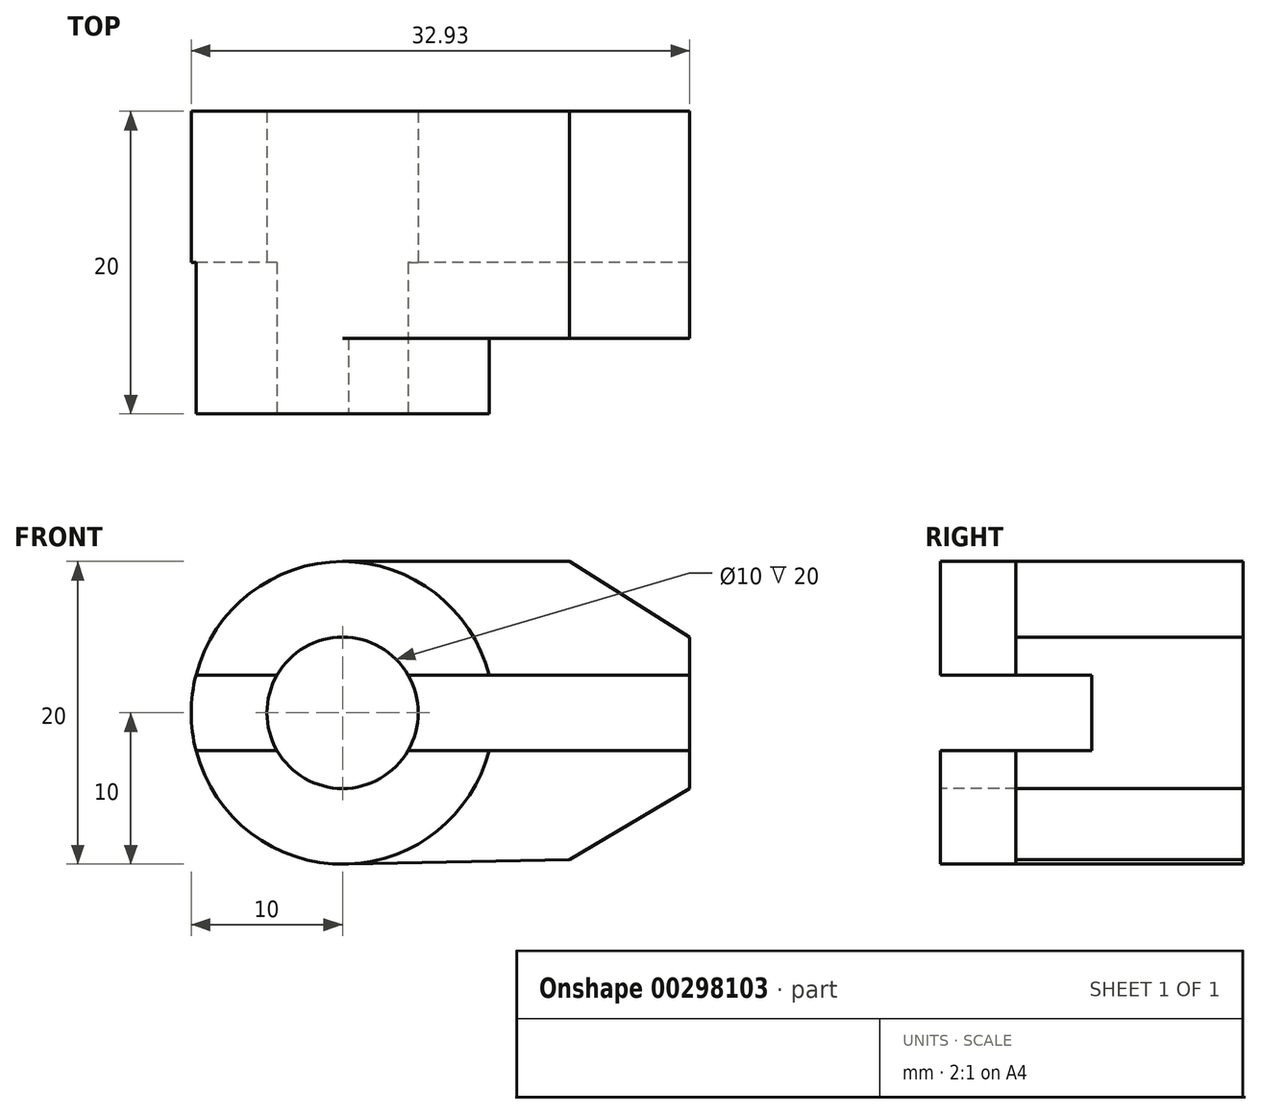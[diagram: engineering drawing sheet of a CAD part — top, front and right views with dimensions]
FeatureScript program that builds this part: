
annotation { "Feature Type Name" : "Feature", "Feature Type Description" : "" }
export const myFeature = defineFeature(function(context is Context, id is Id, definition is map)
    precondition{}
    {
        {
            var Q0;
            Q0=qCreatedBy(makeId("Front.planeOp"),FACE);
            var sketch = newSketch(context, id + "F0", { "sketchPlane" : qUnion([Q0])});
            skCircle(sketch, "E0", {"center": v(0, 0) * mm, "radius": 10 * mm});
            skLineSegment(sketch, "E1", {"start": v(0, 10) * mm, "end": v(15, 10) * mm});
            skPoint(sketch, "E2.end.orphan", {"position": v(0, -10) * mm});
            skLineSegment(sketch, "E3", {"start": v(0, -10) * mm, "end": v(15, -9.7) * mm});
            skLineSegment(sketch, "E4", {"start": v(22.93, 0) * mm, "end": v(22.93, 5) * mm});
            skLineSegment(sketch, "E5", {"start": v(22.93, 5) * mm, "end": v(22.93, 0) * mm});
            skLineSegment(sketch, "E6", {"start": v(22.93, -5) * mm, "end": v(22.93, 0) * mm});
            skLineSegment(sketch, "E7", {"start": v(15, 10) * mm, "end": v(22.93, 5) * mm});
            skLineSegment(sketch, "E8", {"start": v(15, -9.7) * mm, "end": v(22.93, -5) * mm});
            skSolve(sketch);
        }
        {
            var Q0;
            {var subQ0=sQuery(id+"F0.wireOp",EDGE,"E0");var subQ1=makeQuery(id+"F0.imprint","INTERSECT",VERTEX,{"derivedFrom":[subQ0,sQuery(id+"F0.wireOp",EDGE,"E1")]});Q0=makeQuery(id+"F0.imprint","IMPRINT",FACE,{"disambiguationData":[TD([[makeQuery(id+"F0.imprint","IMPRINT",EDGE,{"disambiguationData":[TD([[subQ1,-1.0]])],"derivedFrom":subQ0}),1.0]])]});}
            extrude(context, id + "F1", {"entities" : qUnion([Q0]), "oppositeDirection" : true, "depth" : 20 * mm});
        }
        {
            var Q0;
            {var subQ4=sQuery(id+"F0.wireOp",EDGE,"E1");Q0=makeQuery(id+"F0.imprint","IMPRINT",FACE,{"disambiguationData":[TD([[makeQuery(id+"F0.imprint","IMPRINT",EDGE,{"derivedFrom":subQ4}),-1.0]])]});}
            extrude(context, id + "F2", {"entities" : qUnion([Q0]), "operationType" : NewBodyOperationType.ADD, "oppositeDirection" : true, "depth" : 20 * mm});
        }
        {
            var Q0;
            {var subQ4=sQuery(id+"F0.wireOp",EDGE,"E1");Q0=makeQuery(id+"F0.imprint","IMPRINT",FACE,{"disambiguationData":[TD([[makeQuery(id+"F0.imprint","IMPRINT",EDGE,{"derivedFrom":subQ4}),-1.0]])]});}
            var sketch = newSketch(context, id + "F3", { "sketchPlane" : qUnion([Q0])});
            skArc(sketch, "E9", {"start": v(0, 10) * mm, "mid": v(10, 0) * mm, "end": v(0, -10) * mm});
            skLineSegment(sketch, "E10", {"start": v(0, 10) * mm, "end": v(15, 10) * mm});
            skLineSegment(sketch, "E11", {"start": v(15, 10) * mm, "end": v(22.93, 5) * mm});
            skLineSegment(sketch, "E12", {"start": v(22.93, 5) * mm, "end": v(22.93, -5) * mm});
            skLineSegment(sketch, "E13", {"start": v(22.93, -5) * mm, "end": v(15, -9.7) * mm});
            skLineSegment(sketch, "E14", {"start": v(15, -9.7) * mm, "end": v(0, -10) * mm});
            skSolve(sketch);
        }
        {
            var Q0;
            {var subQ4=sQuery(id+"F3.wireOp",EDGE,"E10");Q0=makeQuery(id+"F3.imprint","IMPRINT",FACE,{"disambiguationData":[TD([[makeQuery(id+"F3.imprint","IMPRINT",EDGE,{"derivedFrom":subQ4}),-1.0]])]});}
            extrude(context, id + "F4", {"entities" : qUnion([Q0]), "operationType" : NewBodyOperationType.REMOVE, "oppositeDirection" : true, "depth" : 5 * mm});
        }
        {
            var Q0;
            {var subQ0=sQuery(id+"F0.wireOp",EDGE,"E0");var subQ1=makeQuery(id+"F0.imprint","INTERSECT",VERTEX,{"derivedFrom":[subQ0,sQuery(id+"F0.wireOp",EDGE,"E1")]});Q0=makeQuery(id+"F0.imprint","IMPRINT",FACE,{"disambiguationData":[TD([[makeQuery(id+"F0.imprint","IMPRINT",EDGE,{"disambiguationData":[TD([[subQ1,-1.0]])],"derivedFrom":subQ0}),1.0]])]});}
            var sketch = newSketch(context, id + "F5", { "sketchPlane" : qUnion([Q0])});
            skCircle(sketch, "E15", {"center": v(0, 0) * mm, "radius": 5 * mm});
            skSolve(sketch);
        }
        {
            var Q0;
            Q0 = qSketchRegion(id + "F5", true);
            extrude(context, id + "F6", {"entities" : qUnion([Q0]), "operationType" : NewBodyOperationType.REMOVE, "endBound" : BoundingType.THROUGH_ALL, "oppositeDirection" : true, "depth" : 25 * mm});
        }
        {
            var Q0;
            {var subQ0=sQuery(id+"F0.wireOp",EDGE,"E0");var subQ1=makeQuery(id+"F0.imprint","INTERSECT",VERTEX,{"derivedFrom":[subQ0,sQuery(id+"F0.wireOp",EDGE,"E1")]});Q0=makeQuery(id+"F0.imprint","IMPRINT",FACE,{"disambiguationData":[TD([[makeQuery(id+"F0.imprint","IMPRINT",EDGE,{"disambiguationData":[TD([[subQ1,-1.0]])],"derivedFrom":subQ0}),1.0]])]});}
            var sketch = newSketch(context, id + "F7", { "sketchPlane" : qUnion([Q0])});
            skLineSegment(sketch, "E16.bottom", {"start": v(25, 2.5) * mm, "end": v(-25, 2.5) * mm});
            skLineSegment(sketch, "E16.top", {"start": v(25, -2.5) * mm, "end": v(-25, -2.5) * mm});
            skLineSegment(sketch, "E16.left", {"start": v(25, 2.5) * mm, "end": v(25, -2.5) * mm});
            skLineSegment(sketch, "E16.right", {"start": v(-25, 2.5) * mm, "end": v(-25, -2.5) * mm});
            skPoint(sketch, "E16.middle", {"position": v(0, 0) * mm});
            skSolve(sketch);
        }
        {
            var Q0;
            {var subQ0=sQuery(id+"F7.wireOp",EDGE,"E16.right");Q0=makeQuery(id+"F7.imprint","IMPRINT",FACE,{"disambiguationData":[TD([[makeQuery(id+"F7.imprint","IMPRINT",EDGE,{"derivedFrom":subQ0}),1.0]])]});}
            var Q1;
            {var subQ0=sQuery(id+"F7.wireOp",EDGE,"E16.bottom");var subQ1=sQuery(id+"F0.wireOp",EDGE,"E0");var subQ2=makeQuery(id+"F0.imprint","INTERSECT",VERTEX,{"derivedFrom":[subQ1,sQuery(id+"F0.wireOp",EDGE,"E1")]});var subQ4=makeQuery(id+"F0.imprint","IMPRINT",EDGE,{"disambiguationData":[TD([[subQ2,1.0]])],"derivedFrom":subQ1});var subQ5=makeQuery(id+"F7.imprint","INTERSECT",VERTEX,{"derivedFrom":[subQ4,subQ0]});Q1=makeQuery(id+"F7.imprint","IMPRINT",FACE,{"disambiguationData":[TD([[makeQuery(id+"F7.imprint","IMPRINT",EDGE,{"disambiguationData":[TD([[subQ5,-1.0]])],"derivedFrom":subQ0}),1.0]])]});}
            var Q2;
            {var subQ0=sQuery(id+"F7.wireOp",EDGE,"E16.left");Q2=makeQuery(id+"F7.imprint","IMPRINT",FACE,{"disambiguationData":[TD([[makeQuery(id+"F7.imprint","IMPRINT",EDGE,{"derivedFrom":subQ0}),-1.0]])]});}
            extrude(context, id + "F8", {"entities" : qUnion([Q0, Q1, Q2]), "operationType" : NewBodyOperationType.REMOVE, "oppositeDirection" : true, "depth" : 10 * mm});
        }
    });
